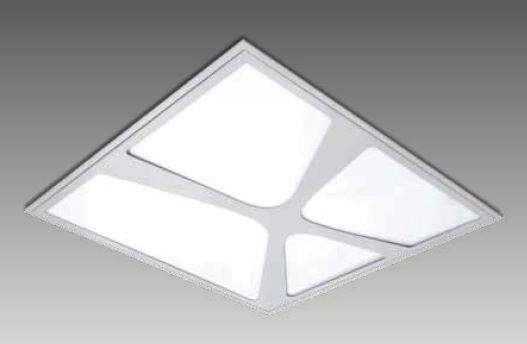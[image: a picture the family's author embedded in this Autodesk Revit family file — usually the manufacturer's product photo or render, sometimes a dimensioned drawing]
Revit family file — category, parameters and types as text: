
# Revit family: G 6060 BOX-9
name_source: partatom
category: Lighting Fixtures
revit_build: Autodesk Revit 2016 (Build: 20150714_1515(x64)
units: mm (PartAtom-declared; Revit-internal decimal feet)

## family parameters
Always vertical = Yes
Cut with Voids When Loaded = No
Host = Ceiling
Light Source = Yes
OmniClass Number = 23.80.70.11
OmniClass Title = Luminaries for Internal Lighting
Part Type = Normal
Room Calculation Point = No
Round Connector Dimension = Use Diameter
Shared = No
Work Plane-Based = No

## types (4) — shared parameters
Color Filter = 16777215
Dimming Lamp Color Temperature Shift = <None>
Emit Shape Visible in Rendering = Yes
Emit from Rectangle Length = 570 mm  [stored 1.87008 ft]
Emit from Rectangle Width = 570 mm  [stored 1.87008 ft]
Light Source Symbol Size = 610 mm
Manufacturer = ARLIGHT
Type Image = G 6060 BOX.JPG

## per-type parameters (varying)
| type | Wattage Comments |
| GBOX.6060.36.30 | 36 |
| GBOX.6060.36.40 | 36 |
| GBOX.6060.28.30 | 28 |
| GBOX.6060.28.40 | 28 |

note: [stored X ft] marks values corroborated as IEEE doubles in the binary element streams (Revit-internal decimal feet)

## geometry (parser evidence)
native form markers: Sweep x3
no freeform markers — native parametric forms only
